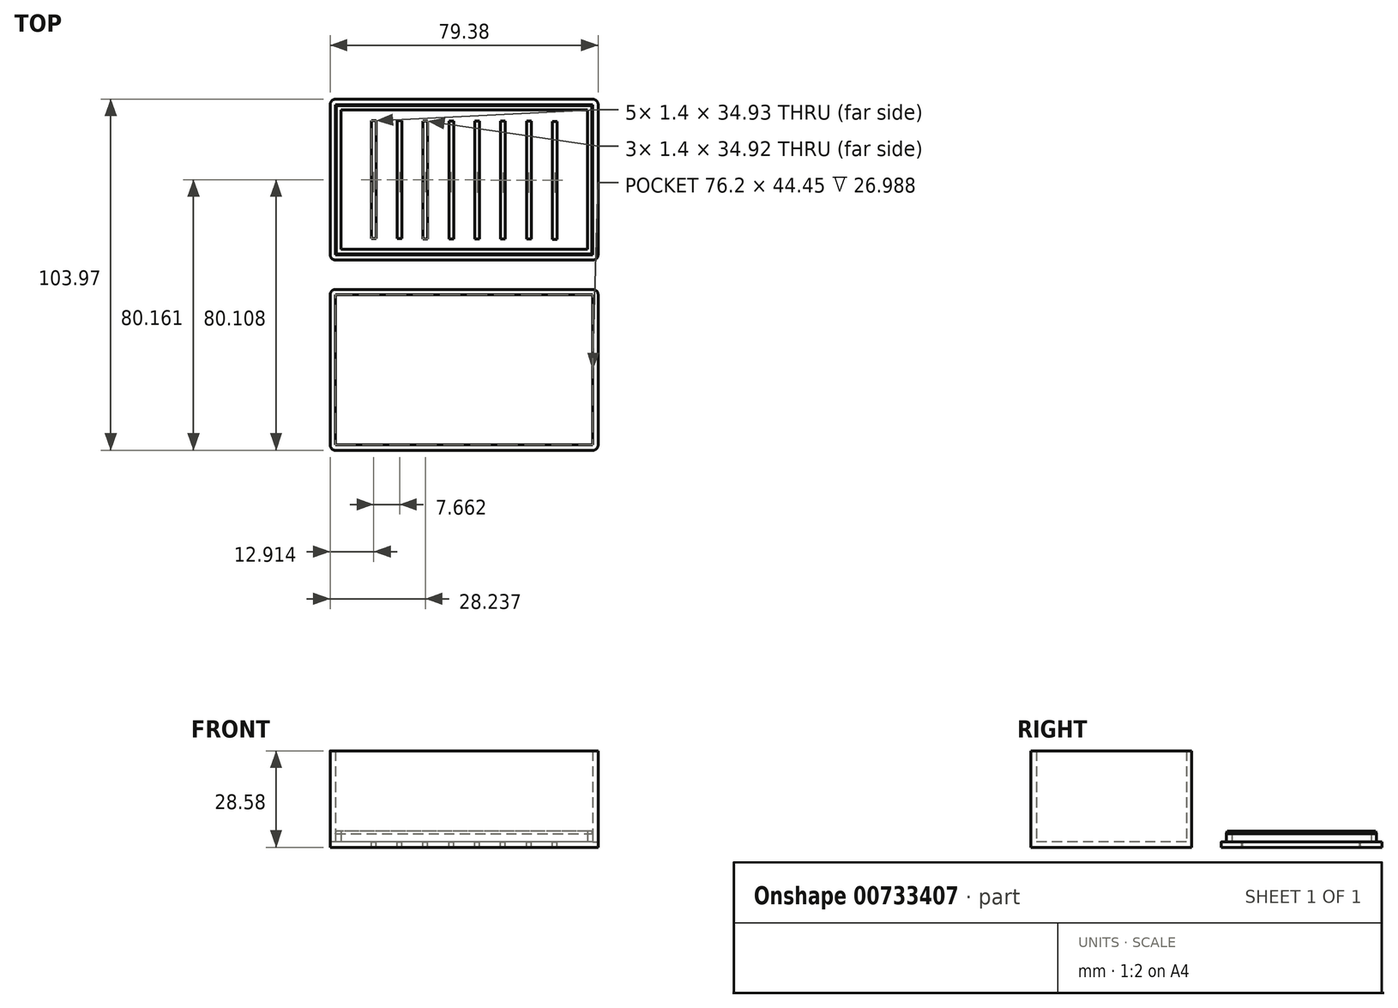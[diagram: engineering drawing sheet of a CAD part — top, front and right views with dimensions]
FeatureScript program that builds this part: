
annotation { "Feature Type Name" : "Feature", "Feature Type Description" : "" }
export const myFeature = defineFeature(function(context is Context, id is Id, definition is map)
    precondition{}
    {
        {
            var Q0;
            Q0=qCreatedBy(makeId("Top.planeOp"),FACE);
            var sketch = newSketch(context, id + "F0", { "sketchPlane" : qUnion([Q0])});
            skLineSegment(sketch, "E0.bottom", {"start": v(38.1, 22.23) * mm, "end": v(-38.1, 22.23) * mm});
            skLineSegment(sketch, "E0.top", {"start": v(38.1, -22.23) * mm, "end": v(-38.1, -22.23) * mm});
            skLineSegment(sketch, "E0.left", {"start": v(38.1, 22.23) * mm, "end": v(38.1, -22.22) * mm});
            skLineSegment(sketch, "E0.right", {"start": v(-38.1, 22.22) * mm, "end": v(-38.1, -22.23) * mm});
            skPoint(sketch, "E0.middle", {"position": v(0, 0) * mm});
            skLineSegment(sketch, "E1.bottom", {"start": v(39.69, -23.81) * mm, "end": v(-39.69, -23.81) * mm});
            skLineSegment(sketch, "E1.top", {"start": v(39.69, 23.81) * mm, "end": v(-39.69, 23.81) * mm});
            skLineSegment(sketch, "E1.left", {"start": v(39.69, -23.81) * mm, "end": v(39.69, 23.81) * mm});
            skLineSegment(sketch, "E1.right", {"start": v(-39.69, -23.81) * mm, "end": v(-39.69, 23.81) * mm});
            skLineSegment(sketch, "E2.bottom", {"start": v(38.1, 78.58) * mm, "end": v(-38.1, 78.58) * mm});
            skLineSegment(sketch, "E2.top", {"start": v(38.1, 34.13) * mm, "end": v(-38.1, 34.13) * mm});
            skLineSegment(sketch, "E2.left", {"start": v(38.1, 78.58) * mm, "end": v(38.1, 34.13) * mm});
            skLineSegment(sketch, "E2.right", {"start": v(-38.1, 78.58) * mm, "end": v(-38.1, 34.13) * mm});
            skPoint(sketch, "E2.middle", {"position": v(0, 56.35) * mm});
            skLineSegment(sketch, "E3.bottom", {"start": v(39.69, 32.54) * mm, "end": v(-39.69, 32.54) * mm});
            skLineSegment(sketch, "E3.top", {"start": v(39.69, 80.16) * mm, "end": v(-39.69, 80.16) * mm});
            skLineSegment(sketch, "E3.left", {"start": v(39.69, 32.54) * mm, "end": v(39.69, 80.16) * mm});
            skLineSegment(sketch, "E3.right", {"start": v(-39.69, 32.54) * mm, "end": v(-39.69, 80.16) * mm});
            skLineSegment(sketch, "E4.bottom", {"start": v(36.51, 76.99) * mm, "end": v(-36.51, 76.99) * mm});
            skLineSegment(sketch, "E4.top", {"start": v(36.51, 35.71) * mm, "end": v(-36.51, 35.71) * mm});
            skLineSegment(sketch, "E4.left", {"start": v(36.51, 76.99) * mm, "end": v(36.51, 35.71) * mm});
            skLineSegment(sketch, "E4.right", {"start": v(-36.51, 76.99) * mm, "end": v(-36.51, 35.71) * mm});
            skSolve(sketch);
        }
        {
            var Q0;
            Q0=makeQuery(id+"F0.imprint","IMPRINT",FACE,{"disambiguationData":[TD([[makeQuery(id+"F0.imprint","IMPRINT",EDGE,{"derivedFrom":sQuery(id+"F0.wireOp",EDGE,"E0.bottom")}),-1.0]])]});
            var Q1;
            Q1=makeQuery(id+"F0.imprint","IMPRINT",FACE,{"disambiguationData":[TD([[makeQuery(id+"F0.imprint","IMPRINT",EDGE,{"derivedFrom":sQuery(id+"F0.wireOp",EDGE,"E0.bottom")}),1.0]])]});
            var Q2;
            Q2=makeQuery(id+"F0.imprint","IMPRINT",FACE,{"disambiguationData":[TD([[makeQuery(id+"F0.imprint","IMPRINT",EDGE,{"derivedFrom":sQuery(id+"F0.wireOp",EDGE,"E2.bottom")}),-1.0]])]});
            var Q3;
            Q3=makeQuery(id+"F0.imprint","IMPRINT",FACE,{"disambiguationData":[TD([[makeQuery(id+"F0.imprint","IMPRINT",EDGE,{"derivedFrom":sQuery(id+"F0.wireOp",EDGE,"E2.bottom")}),1.0]])]});
            var Q4;
            Q4=makeQuery(id+"F0.imprint","IMPRINT",FACE,{"disambiguationData":[TD([[makeQuery(id+"F0.imprint","IMPRINT",EDGE,{"derivedFrom":sQuery(id+"F0.wireOp",EDGE,"E4.bottom")}),1.0]])]});
            extrude(context, id + "F1", {"entities" : qUnion([Q0, Q1, Q2, Q3, Q4]), "oppositeDirection" : true, "depth" : 1.59 * mm, "offsetDistance" : 25.4 * mm});
        }
        {
            var Q0;
            Q0=makeQuery(id+"F0.imprint","IMPRINT",FACE,{"disambiguationData":[TD([[makeQuery(id+"F0.imprint","IMPRINT",EDGE,{"derivedFrom":sQuery(id+"F0.wireOp",EDGE,"E0.bottom")}),-1.0]])]});
            extrude(context, id + "F2", {"entities" : qUnion([Q0]), "operationType" : NewBodyOperationType.ADD, "depth" : 26.99 * mm, "offsetDistance" : 25.4 * mm});
        }
        {
            var Q0;
            Q0=makeQuery(id+"F0.imprint","IMPRINT",FACE,{"disambiguationData":[TD([[makeQuery(id+"F0.imprint","IMPRINT",EDGE,{"derivedFrom":sQuery(id+"F0.wireOp",EDGE,"E2.bottom")}),1.0]])]});
            extrude(context, id + "F3", {"entities" : qUnion([Q0]), "operationType" : NewBodyOperationType.ADD, "depth" : 3.17 * mm, "offsetDistance" : 25.4 * mm});
        }
        {
            var Q0;
            Q0=makeQuery(id+"F1.opExtrude","SWEPT_EDGE",EDGE,{"disambiguationData":[OSD([sQuery(id+"F0.wireOp",EDGE,"E3.top"),sQuery(id+"F0.wireOp",EDGE,"E3.right")])]});
            var Q1;
            Q1=makeQuery(id+"F1.opExtrude","SWEPT_EDGE",EDGE,{"disambiguationData":[OSD([sQuery(id+"F0.wireOp",EDGE,"E3.bottom"),sQuery(id+"F0.wireOp",EDGE,"E3.right")])]});
            var Q2;
            {var subQ0=sQuery(id+"F0.wireOp",EDGE,"E1.left");var subQ1=sQuery(id+"F0.wireOp",EDGE,"E1.top");Q2=makeQuery(id+"F2.boolean.opBoolean","MERGE",EDGE,{"derivedFrom":[makeQuery(id+"F1.opExtrude","SWEPT_EDGE",EDGE,{"disambiguationData":[OSD([subQ1,subQ0])]}),makeQuery(id+"F2.opExtrude","SWEPT_EDGE",EDGE,{"disambiguationData":[OSD([subQ1,subQ0])]})]});}
            var Q3;
            {var subQ0=sQuery(id+"F0.wireOp",EDGE,"E1.right");var subQ1=sQuery(id+"F0.wireOp",EDGE,"E1.top");Q3=makeQuery(id+"F2.boolean.opBoolean","MERGE",EDGE,{"derivedFrom":[makeQuery(id+"F1.opExtrude","SWEPT_EDGE",EDGE,{"disambiguationData":[OSD([subQ1,subQ0])]}),makeQuery(id+"F2.opExtrude","SWEPT_EDGE",EDGE,{"disambiguationData":[OSD([subQ1,subQ0])]})]});}
            var Q4;
            Q4=makeQuery(id+"F1.opExtrude","SWEPT_EDGE",EDGE,{"disambiguationData":[OSD([sQuery(id+"F0.wireOp",EDGE,"E3.top"),sQuery(id+"F0.wireOp",EDGE,"E3.left")])]});
            var Q5;
            Q5=makeQuery(id+"F1.opExtrude","SWEPT_EDGE",EDGE,{"disambiguationData":[OSD([sQuery(id+"F0.wireOp",EDGE,"E3.bottom"),sQuery(id+"F0.wireOp",EDGE,"E3.left")])]});
            var Q6;
            {var subQ0=sQuery(id+"F0.wireOp",EDGE,"E1.left");var subQ1=sQuery(id+"F0.wireOp",EDGE,"E1.bottom");Q6=makeQuery(id+"F2.boolean.opBoolean","MERGE",EDGE,{"derivedFrom":[makeQuery(id+"F1.opExtrude","SWEPT_EDGE",EDGE,{"disambiguationData":[OSD([subQ1,subQ0])]}),makeQuery(id+"F2.opExtrude","SWEPT_EDGE",EDGE,{"disambiguationData":[OSD([subQ1,subQ0])]})]});}
            var Q7;
            {var subQ0=sQuery(id+"F0.wireOp",EDGE,"E1.right");var subQ1=sQuery(id+"F0.wireOp",EDGE,"E1.bottom");Q7=makeQuery(id+"F2.boolean.opBoolean","MERGE",EDGE,{"derivedFrom":[makeQuery(id+"F1.opExtrude","SWEPT_EDGE",EDGE,{"disambiguationData":[OSD([subQ1,subQ0])]}),makeQuery(id+"F2.opExtrude","SWEPT_EDGE",EDGE,{"disambiguationData":[OSD([subQ1,subQ0])]})]});}
            fillet(context, id + "F4", {"entities" : qUnion([Q0, Q1, Q2, Q3, Q4, Q5, Q6, Q7]), "radius" : 1.59 * mm, "tangentPropagation" : true, "allowEdgeOverflow" : false});
        }
        {
            var Q0;
            Q0=makeQuery(id+"F3.opExtrude","CAP_EDGE",EDGE,{"disambiguationData":[OSD([sQuery(id+"F0.wireOp",EDGE,"E2.bottom")])],"isStart":false});
            var Q1;
            Q1=makeQuery(id+"F3.opExtrude","CAP_EDGE",EDGE,{"disambiguationData":[OSD([sQuery(id+"F0.wireOp",EDGE,"E2.left")])],"isStart":false});
            var Q2;
            Q2=makeQuery(id+"F3.opExtrude","CAP_EDGE",EDGE,{"disambiguationData":[OSD([sQuery(id+"F0.wireOp",EDGE,"E2.top")])],"isStart":false});
            var Q3;
            Q3=makeQuery(id+"F3.opExtrude","CAP_EDGE",EDGE,{"disambiguationData":[OSD([sQuery(id+"F0.wireOp",EDGE,"E2.right")])],"isStart":false});
            chamfer(context, id + "F5", {"entities" : qUnion([Q0, Q1, Q2, Q3]), "chamferType" : ChamferType.TWO_OFFSETS, "width1" : 0.25 * mm, "oppositeDirection" : false, "width2" : 0.8 * mm, "tangentPropagation" : true});
        }
        {
            var Q0;
            Q0=qCreatedBy(makeId("Top.planeOp"),FACE);
            var sketch = newSketch(context, id + "F6", { "sketchPlane" : qUnion([Q0])});
            skLineSegment(sketch, "E5.bottom", {"start": v(-27.47, 73.81) * mm, "end": v(-26.08, 73.81) * mm});
            skLineSegment(sketch, "E5.top", {"start": v(-27.47, 38.89) * mm, "end": v(-26.08, 38.89) * mm});
            skLineSegment(sketch, "E5.left", {"start": v(-27.47, 73.81) * mm, "end": v(-27.47, 38.89) * mm});
            skLineSegment(sketch, "E5.right", {"start": v(-26.08, 73.81) * mm, "end": v(-26.08, 38.89) * mm});
            skLineSegment(sketch, "E6.1.0.0", {"start": v(-18.42, 73.79) * mm, "end": v(-18.42, 38.86) * mm});
            skLineSegment(sketch, "E6.1.0.1", {"start": v(-19.81, 73.79) * mm, "end": v(-19.81, 38.86) * mm});
            skLineSegment(sketch, "E6.1.0.2", {"start": v(-19.81, 73.79) * mm, "end": v(-18.42, 73.79) * mm});
            skLineSegment(sketch, "E6.1.0.3", {"start": v(-19.81, 38.86) * mm, "end": v(-18.42, 38.86) * mm});
            skLineSegment(sketch, "E6.2.0.0", {"start": v(-10.75, 73.76) * mm, "end": v(-10.75, 38.84) * mm});
            skLineSegment(sketch, "E6.2.0.1", {"start": v(-12.15, 73.76) * mm, "end": v(-12.15, 38.84) * mm});
            skLineSegment(sketch, "E6.2.0.2", {"start": v(-12.15, 73.76) * mm, "end": v(-10.75, 73.76) * mm});
            skLineSegment(sketch, "E6.2.0.3", {"start": v(-12.15, 38.84) * mm, "end": v(-10.75, 38.84) * mm});
            skLineSegment(sketch, "E6.3.0.0", {"start": v(-3.1, 73.73) * mm, "end": v(-3.1, 38.8) * mm});
            skLineSegment(sketch, "E6.3.0.1", {"start": v(-4.49, 73.73) * mm, "end": v(-4.49, 38.8) * mm});
            skLineSegment(sketch, "E6.3.0.2", {"start": v(-4.49, 73.73) * mm, "end": v(-3.1, 73.73) * mm});
            skLineSegment(sketch, "E6.3.0.3", {"start": v(-4.49, 38.8) * mm, "end": v(-3.1, 38.8) * mm});
            skLineSegment(sketch, "E6.4.0.0", {"start": v(4.57, 73.7) * mm, "end": v(4.57, 38.78) * mm});
            skLineSegment(sketch, "E6.4.0.1", {"start": v(3.17, 73.7) * mm, "end": v(3.17, 38.78) * mm});
            skLineSegment(sketch, "E6.4.0.2", {"start": v(3.17, 73.7) * mm, "end": v(4.57, 73.7) * mm});
            skLineSegment(sketch, "E6.4.0.3", {"start": v(3.17, 38.78) * mm, "end": v(4.57, 38.78) * mm});
            skLineSegment(sketch, "E6.5.0.0", {"start": v(12.23, 73.68) * mm, "end": v(12.23, 38.75) * mm});
            skLineSegment(sketch, "E6.5.0.1", {"start": v(10.84, 73.68) * mm, "end": v(10.84, 38.75) * mm});
            skLineSegment(sketch, "E6.5.0.2", {"start": v(10.84, 73.68) * mm, "end": v(12.23, 73.68) * mm});
            skLineSegment(sketch, "E6.5.0.3", {"start": v(10.84, 38.75) * mm, "end": v(12.23, 38.75) * mm});
            skLineSegment(sketch, "E6.6.0.0", {"start": v(19.9, 73.65) * mm, "end": v(19.9, 38.73) * mm});
            skLineSegment(sketch, "E6.6.0.1", {"start": v(18.5, 73.65) * mm, "end": v(18.5, 38.73) * mm});
            skLineSegment(sketch, "E6.6.0.2", {"start": v(18.5, 73.65) * mm, "end": v(19.9, 73.65) * mm});
            skLineSegment(sketch, "E6.6.0.3", {"start": v(18.5, 38.73) * mm, "end": v(19.9, 38.73) * mm});
            skLineSegment(sketch, "E6.7.0.0", {"start": v(27.55, 73.63) * mm, "end": v(27.55, 38.7) * mm});
            skLineSegment(sketch, "E6.7.0.1", {"start": v(26.16, 73.63) * mm, "end": v(26.16, 38.7) * mm});
            skLineSegment(sketch, "E6.7.0.2", {"start": v(26.16, 73.63) * mm, "end": v(27.55, 73.63) * mm});
            skLineSegment(sketch, "E6.7.0.3", {"start": v(26.16, 38.7) * mm, "end": v(27.55, 38.7) * mm});
            skLineSegment(sketch, "E6.direction1", {"start": v(-27.47, 38.89) * mm, "end": v(-19.81, 38.86) * mm, "construction": true});
            skSolve(sketch);
        }
        {
            var Q0;
            Q0 = qSketchRegion(id + "F6", true);
            extrude(context, id + "F7", {"entities" : qUnion([Q0]), "operationType" : NewBodyOperationType.REMOVE, "endBound" : BoundingType.UP_TO_NEXT, "oppositeDirection" : true, "depth" : 25.4 * mm, "offsetDistance" : 25.4 * mm});
        }
    });
